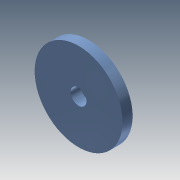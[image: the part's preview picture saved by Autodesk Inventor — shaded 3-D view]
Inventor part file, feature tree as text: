
AUTODESK INVENTOR PART (.ipt)
format: ipt  version: 2013 (Build 170138000, 138)  size: 112,128 bytes
history: native  units: mm
features: extrude x6, sketch x6
ambient origin geometry x8: Origin, YZ Plane, XZ Plane, XY Plane, X Axis, Y Axis, Z Axis, Center Point
bodies: Solid1 (feature_tree)
feature tree (12):
  extrude  "Extrusion1"  Depth=3.8mm TaperAngle=0.0deg
  extrude  "Extrusion2"  Depth=1.0mm TaperAngle=0.0deg
  extrude  "Extrusion3"  Depth=3.8mm TaperAngle=0.0deg
  extrude  "Extrusion4"  Depth=3.6mm TaperAngle=0.0deg
  extrude  "Extrusion5"  Depth=3.6mm TaperAngle=0.0deg
  extrude  "Extrusion6"  Depth=3.8mm TaperAngle=0.0deg
  sketch  "Sketch1"  dims[d0=33.15mm d1=3.8mm d2=0.0mm]
  sketch  "Sketch2"  dims[d3=28.0mm d4=1.0mm d5=0.0mm]
  sketch  "Sketch3"  dims[d6=10.0mm d7=3.8mm d8=0.0mm]
  sketch  "Sketch4"  dims[d9=3.6mm d10=3.6mm d11=0.0mm]
  sketch  "Sketch5"  dims[d12=6.0mm d13=3.6mm d14=0.0mm]
  sketch  "Sketch6"  dims[d15=6.0mm d16=3.8mm d17=0.0mm]
